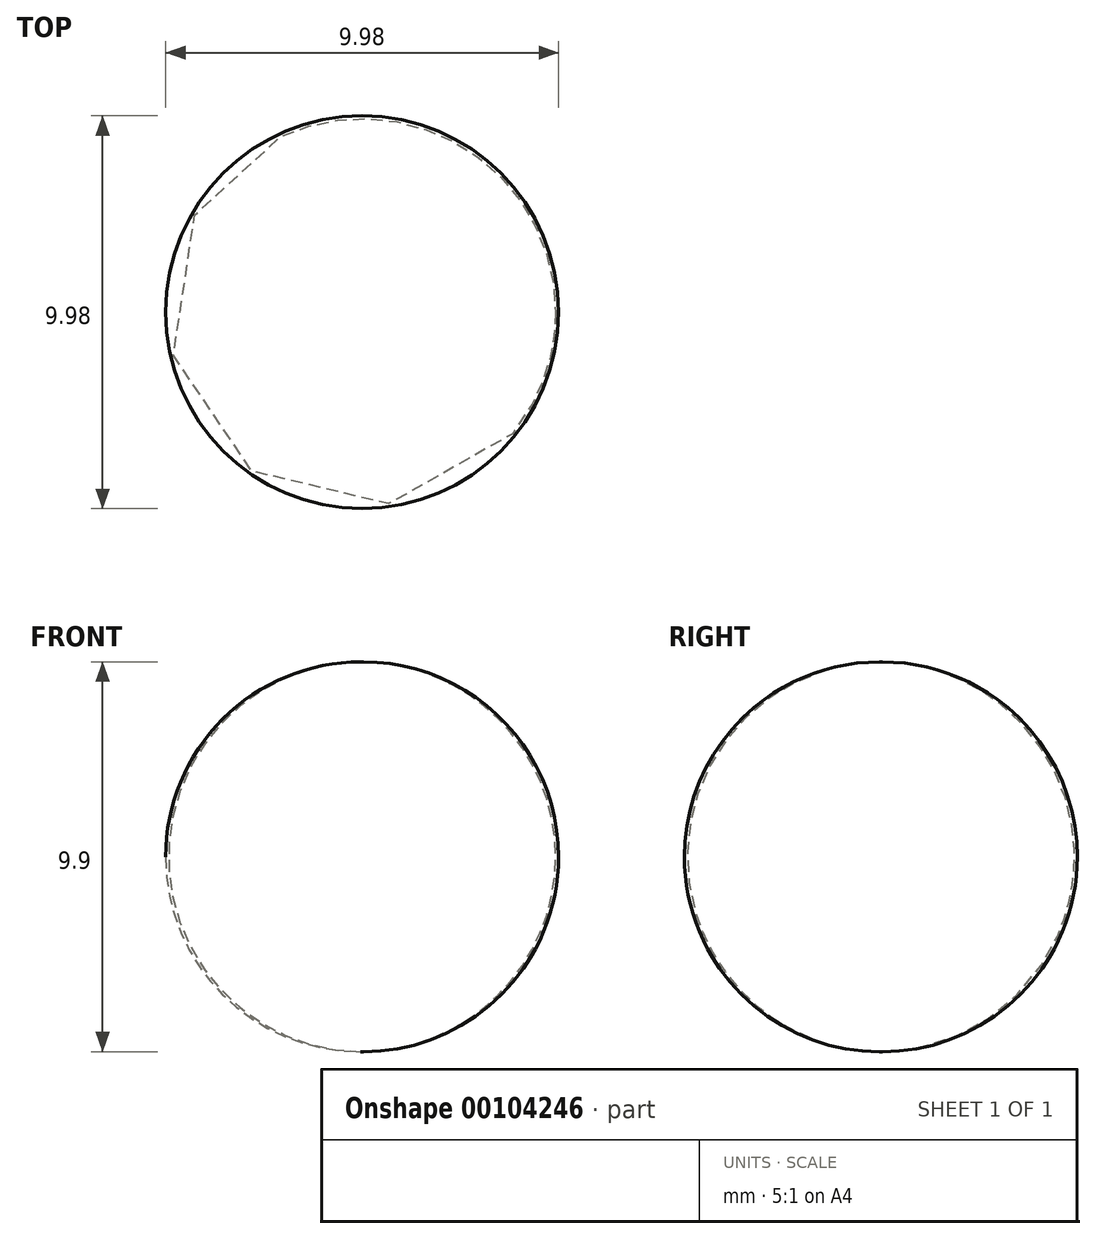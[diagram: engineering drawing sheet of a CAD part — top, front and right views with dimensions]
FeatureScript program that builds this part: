
annotation { "Feature Type Name" : "Feature", "Feature Type Description" : "" }
export const myFeature = defineFeature(function(context is Context, id is Id, definition is map)
    precondition{}
    {
        {
            var Q0;
            Q0=qCreatedBy(makeId("Front.planeOp"),FACE);
            var sketch = newSketch(context, id + "F0", { "sketchPlane" : qUnion([Q0])});
            skLineSegment(sketch, "E0", {"start": v(0, 5.15) * mm, "end": v(0, -4.75) * mm});
            skArc(sketch, "E1", {"start": v(0, -4.75) * mm, "mid": v(4.92, 0.2) * mm, "end": v(0, 5.15) * mm});
            skSolve(sketch);
        }
        {
            var Q0;
            Q0=sQuery(id+"F0.wireOp",EDGE,"E1");
            var Q1;
            Q1=sQuery(id+"F0.wireOp",EDGE,"E0");
            revolve(context, id + "F1", {"bodyType" : ToolBodyType.SURFACE, "surfaceEntities" : qUnion([Q0]), "axis" : qUnion([Q1]), "revolveType" : RevolveType.FULL});
        }
    });
